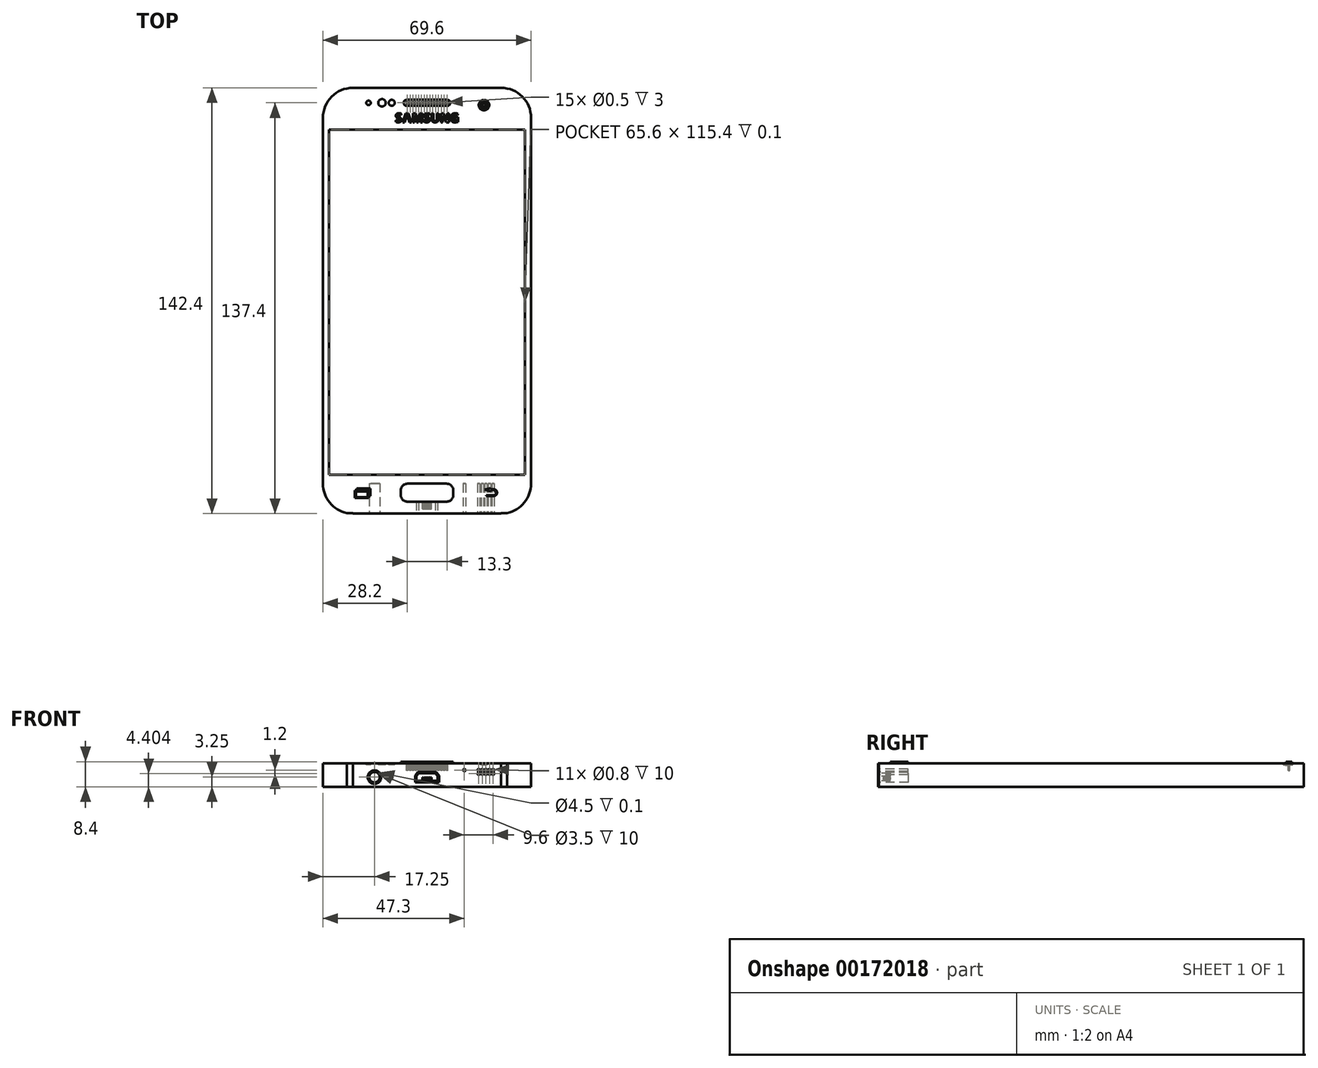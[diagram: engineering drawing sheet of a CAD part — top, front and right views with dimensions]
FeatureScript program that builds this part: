
annotation { "Feature Type Name" : "Feature", "Feature Type Description" : "" }
export const myFeature = defineFeature(function(context is Context, id is Id, definition is map)
    precondition{}
    {
        {
            var Q0;
            Q0=qCreatedBy(makeId("Top.planeOp"),FACE);
            var sketch = newSketch(context, id + "F0", { "sketchPlane" : qUnion([Q0])});
            skLineSegment(sketch, "E0.bottom", {"start": v(0, 0) * mm, "end": v(69.6, 0) * mm});
            skLineSegment(sketch, "E0.top", {"start": v(0, -142.4) * mm, "end": v(69.6, -142.4) * mm});
            skLineSegment(sketch, "E0.left", {"start": v(0, 0) * mm, "end": v(0, -142.4) * mm});
            skLineSegment(sketch, "E0.right", {"start": v(69.6, 0) * mm, "end": v(69.6, -142.4) * mm});
            skSolve(sketch);
        }
        {
            var Q0;
            Q0 = qSketchRegion(id + "F0", true);
            extrude(context, id + "F1", {"entities" : qUnion([Q0]), "depth" : 7.9 * mm});
        }
        {
            var Q0;
            Q0=makeQuery(id+"F1.opExtrude","SWEPT_EDGE",EDGE,{"disambiguationData":[OSD([sQuery(id+"F0.wireOp",EDGE,"E0.top"),sQuery(id+"F0.wireOp",EDGE,"E0.right")])]});
            var Q1;
            Q1=makeQuery(id+"F1.opExtrude","SWEPT_EDGE",EDGE,{"disambiguationData":[OSD([sQuery(id+"F0.wireOp",EDGE,"E0.top"),sQuery(id+"F0.wireOp",EDGE,"E0.left")])]});
            var Q2;
            Q2=makeQuery(id+"F1.opExtrude","SWEPT_EDGE",EDGE,{"disambiguationData":[OSD([sQuery(id+"F0.wireOp",EDGE,"E0.bottom"),sQuery(id+"F0.wireOp",EDGE,"E0.right")])]});
            var Q3;
            Q3=makeQuery(id+"F1.opExtrude","SWEPT_EDGE",EDGE,{"disambiguationData":[OSD([sQuery(id+"F0.wireOp",EDGE,"E0.bottom"),sQuery(id+"F0.wireOp",EDGE,"E0.left")])]});
            fillet(context, id + "F2", {"entities" : qUnion([Q0, Q1, Q2, Q3]), "radius" : 10 * mm, "tangentPropagation" : true, "allowEdgeOverflow" : false});
        }
        {
            var Q0;
            Q0=makeQuery(id+"F1.opExtrude","CAP_FACE",FACE,{"disambiguationData":[OSD([sQuery(id+"F0.wireOp",EDGE,"E0.bottom"),sQuery(id+"F0.wireOp",EDGE,"E0.top"),sQuery(id+"F0.wireOp",EDGE,"E0.left"),sQuery(id+"F0.wireOp",EDGE,"E0.right")])],"isStart":false});
            var sketch = newSketch(context, id + "F3", { "sketchPlane" : qUnion([Q0])});
            skLineSegment(sketch, "E1.bottom", {"start": v(2, -14) * mm, "end": v(67.6, -14) * mm});
            skLineSegment(sketch, "E1.top", {"start": v(2, -129.4) * mm, "end": v(67.6, -129.4) * mm});
            skLineSegment(sketch, "E1.left", {"start": v(2, -14) * mm, "end": v(2, -129.4) * mm});
            skLineSegment(sketch, "E1.right", {"start": v(67.6, -14) * mm, "end": v(67.6, -129.4) * mm});
            skSolve(sketch);
        }
        {
            var Q0;
            Q0=makeQuery(id+"F3.imprint","IMPRINT",FACE,{"disambiguationData":[TD([[makeQuery(id+"F3.imprint","IMPRINT",EDGE,{"derivedFrom":sQuery(id+"F3.wireOp",EDGE,"E1.bottom")}),1.0]])]});
            var sketch = newSketch(context, id + "F4", { "sketchPlane" : qUnion([Q0])});
            skLineSegment(sketch, "E2.bottom", {"start": v(26, -132.4) * mm, "end": v(43.6, -132.4) * mm});
            skLineSegment(sketch, "E2.top", {"start": v(26, -138.4) * mm, "end": v(43.6, -138.4) * mm});
            skLineSegment(sketch, "E2.left", {"start": v(26, -132.4) * mm, "end": v(26, -138.4) * mm});
            skLineSegment(sketch, "E2.right", {"start": v(43.6, -132.4) * mm, "end": v(43.6, -138.4) * mm});
            skSolve(sketch);
        }
        {
            var Q0;
            Q0 = qSketchRegion(id + "F4", true);
            extrude(context, id + "F5", {"entities" : qUnion([Q0]), "operationType" : NewBodyOperationType.ADD, "depth" : 0.5 * mm});
        }
        {
            var Q0;
            Q0=makeQuery(id+"F5.opExtrude","SWEPT_EDGE",EDGE,{"disambiguationData":[OSD([sQuery(id+"F4.wireOp",EDGE,"E2.bottom"),sQuery(id+"F4.wireOp",EDGE,"E2.left")])]});
            var Q1;
            Q1=makeQuery(id+"F5.opExtrude","SWEPT_EDGE",EDGE,{"disambiguationData":[OSD([sQuery(id+"F4.wireOp",EDGE,"E2.bottom"),sQuery(id+"F4.wireOp",EDGE,"E2.right")])]});
            var Q2;
            Q2=makeQuery(id+"F5.opExtrude","SWEPT_EDGE",EDGE,{"disambiguationData":[OSD([sQuery(id+"F4.wireOp",EDGE,"E2.top"),sQuery(id+"F4.wireOp",EDGE,"E2.left")])]});
            var Q3;
            Q3=makeQuery(id+"F5.opExtrude","SWEPT_EDGE",EDGE,{"disambiguationData":[OSD([sQuery(id+"F4.wireOp",EDGE,"E2.top"),sQuery(id+"F4.wireOp",EDGE,"E2.right")])]});
            fillet(context, id + "F6", {"entities" : qUnion([Q0, Q1, Q2, Q3]), "radius" : 2.25 * mm, "tangentPropagation" : true, "allowEdgeOverflow" : false});
        }
        {
            var Q0;
            Q0 = qSketchRegion(id + "F3", true);
            extrude(context, id + "F7", {"entities" : qUnion([Q0]), "operationType" : NewBodyOperationType.REMOVE, "oppositeDirection" : true, "depth" : 0.1 * mm});
        }
        {
            var Q0;
            Q0=makeQuery(id+"F1.opExtrude","CAP_FACE",FACE,{"disambiguationData":[OSD([sQuery(id+"F0.wireOp",EDGE,"E0.bottom"),sQuery(id+"F0.wireOp",EDGE,"E0.top"),sQuery(id+"F0.wireOp",EDGE,"E0.left"),sQuery(id+"F0.wireOp",EDGE,"E0.right")])],"isStart":false});
            var sketch = newSketch(context, id + "F8", { "sketchPlane" : qUnion([Q0])});
            skLineSegment(sketch, "E3.bottom", {"start": v(27, -4) * mm, "end": v(42.6, -4) * mm});
            skLineSegment(sketch, "E3.top", {"start": v(27, -6) * mm, "end": v(42.6, -6) * mm});
            skLineSegment(sketch, "E3.left", {"start": v(27, -4) * mm, "end": v(27, -6) * mm});
            skLineSegment(sketch, "E3.right", {"start": v(42.6, -4) * mm, "end": v(42.6, -6) * mm});
            skSolve(sketch);
        }
        {
            var Q0;
            Q0 = qSketchRegion(id + "F8", true);
            extrude(context, id + "F9", {"entities" : qUnion([Q0]), "operationType" : NewBodyOperationType.ADD, "depth" : 0.5 * mm});
        }
        {
            var Q0;
            Q0=makeQuery(id+"F9.opExtrude","SWEPT_EDGE",EDGE,{"disambiguationData":[OSD([sQuery(id+"F8.wireOp",EDGE,"E3.bottom"),sQuery(id+"F8.wireOp",EDGE,"E3.right")])]});
            var Q1;
            Q1=makeQuery(id+"F9.opExtrude","SWEPT_EDGE",EDGE,{"disambiguationData":[OSD([sQuery(id+"F8.wireOp",EDGE,"E3.bottom"),sQuery(id+"F8.wireOp",EDGE,"E3.left")])]});
            var Q2;
            Q2=makeQuery(id+"F9.opExtrude","SWEPT_EDGE",EDGE,{"disambiguationData":[OSD([sQuery(id+"F8.wireOp",EDGE,"E3.top"),sQuery(id+"F8.wireOp",EDGE,"E3.right")])]});
            var Q3;
            Q3=makeQuery(id+"F9.opExtrude","SWEPT_EDGE",EDGE,{"disambiguationData":[OSD([sQuery(id+"F8.wireOp",EDGE,"E3.top"),sQuery(id+"F8.wireOp",EDGE,"E3.left")])]});
            fillet(context, id + "F10", {"entities" : qUnion([Q0, Q1, Q2, Q3]), "radius" : 1 * mm, "tangentPropagation" : true, "allowEdgeOverflow" : false});
        }
        {
            var Q0;
            Q0=makeQuery(id+"F1.opExtrude","CAP_FACE",FACE,{"disambiguationData":[OSD([sQuery(id+"F0.wireOp",EDGE,"E0.bottom"),sQuery(id+"F0.wireOp",EDGE,"E0.top"),sQuery(id+"F0.wireOp",EDGE,"E0.left"),sQuery(id+"F0.wireOp",EDGE,"E0.right")])],"isStart":false});
            var sketch = newSketch(context, id + "F11", { "sketchPlane" : qUnion([Q0])});
            skCircle(sketch, "E4", {"center": v(23, -5) * mm, "radius": 1 * mm});
            skCircle(sketch, "E5", {"center": v(19.75, -5) * mm, "radius": 1.25 * mm});
            skCircle(sketch, "E6", {"center": v(15.25, -5) * mm, "radius": 0.75 * mm});
            skSolve(sketch);
        }
        {
            var Q0;
            Q0 = qSketchRegion(id + "F11", true);
            extrude(context, id + "F12", {"entities" : qUnion([Q0]), "operationType" : NewBodyOperationType.REMOVE, "oppositeDirection" : true, "depth" : 0.5 * mm});
        }
        {
            var Q0;
            Q0=makeQuery(id+"F9.opExtrude","CAP_FACE",FACE,{"disambiguationData":[OSD([sQuery(id+"F8.wireOp",EDGE,"E3.bottom"),sQuery(id+"F8.wireOp",EDGE,"E3.top"),sQuery(id+"F8.wireOp",EDGE,"E3.left"),sQuery(id+"F8.wireOp",EDGE,"E3.right")])],"isStart":false});
            var sketch = newSketch(context, id + "F13", { "sketchPlane" : qUnion([Q0])});
            skCircle(sketch, "E7", {"center": v(28.2, -5) * mm, "radius": 0.25 * mm});
            skPoint(sketch, "E7.centerSnap0", {"position": v(28.2, -4) * mm});
            skPoint(sketch, "E7.centerSnap1", {"position": v(27, -5) * mm});
            skCircle(sketch, "E8.1.0.0", {"center": v(29.15, -5) * mm, "radius": 0.25 * mm});
            skCircle(sketch, "E8.2.0.0", {"center": v(30.1, -5) * mm, "radius": 0.25 * mm});
            skCircle(sketch, "E8.3.0.0", {"center": v(31.05, -5) * mm, "radius": 0.25 * mm});
            skCircle(sketch, "E8.4.0.0", {"center": v(32, -5) * mm, "radius": 0.25 * mm});
            skCircle(sketch, "E8.5.0.0", {"center": v(32.95, -5) * mm, "radius": 0.25 * mm});
            skCircle(sketch, "E8.6.0.0", {"center": v(33.9, -5) * mm, "radius": 0.25 * mm});
            skCircle(sketch, "E8.7.0.0", {"center": v(34.85, -5) * mm, "radius": 0.25 * mm});
            skCircle(sketch, "E8.8.0.0", {"center": v(35.8, -5) * mm, "radius": 0.25 * mm});
            skCircle(sketch, "E8.9.0.0", {"center": v(36.75, -5) * mm, "radius": 0.25 * mm});
            skCircle(sketch, "E8.10.0.0", {"center": v(37.7, -5) * mm, "radius": 0.25 * mm});
            skCircle(sketch, "E8.11.0.0", {"center": v(38.65, -5) * mm, "radius": 0.25 * mm});
            skCircle(sketch, "E8.12.0.0", {"center": v(39.6, -5) * mm, "radius": 0.25 * mm});
            skCircle(sketch, "E8.13.0.0", {"center": v(40.55, -5) * mm, "radius": 0.25 * mm});
            skCircle(sketch, "E8.14.0.0", {"center": v(41.5, -5) * mm, "radius": 0.25 * mm});
            skLineSegment(sketch, "E8.direction1", {"start": v(28.2, -5) * mm, "end": v(29.15, -5) * mm, "construction": true});
            skSolve(sketch);
        }
        {
            var Q0;
            Q0 = qSketchRegion(id + "F13", true);
            extrude(context, id + "F14", {"entities" : qUnion([Q0]), "operationType" : NewBodyOperationType.REMOVE, "oppositeDirection" : true, "depth" : 3 * mm});
        }
        {
            var Q0;
            Q0=makeQuery(id+"F1.opExtrude","CAP_FACE",FACE,{"disambiguationData":[OSD([sQuery(id+"F0.wireOp",EDGE,"E0.bottom"),sQuery(id+"F0.wireOp",EDGE,"E0.top"),sQuery(id+"F0.wireOp",EDGE,"E0.left"),sQuery(id+"F0.wireOp",EDGE,"E0.right")])],"isStart":false});
            var sketch = newSketch(context, id + "F15", { "sketchPlane" : qUnion([Q0])});
            skCircle(sketch, "E9", {"center": v(53.85, -5.75) * mm, "radius": 1.75 * mm});
            skSolve(sketch);
        }
        {
            var Q0;
            Q0 = qSketchRegion(id + "F15", true);
            extrude(context, id + "F16", {"entities" : qUnion([Q0]), "operationType" : NewBodyOperationType.REMOVE, "oppositeDirection" : true, "depth" : 0.1 * mm});
        }
        {
            var Q0;
            Q0=makeQuery(id+"F16.boolean.opBoolean","COPY",FACE,{"derivedFrom":makeQuery(id+"F16.opExtrude","CAP_FACE",FACE,{"disambiguationData":[OSD([sQuery(id+"F15.wireOp",EDGE,"E9")])],"isStart":false})});
            var sketch = newSketch(context, id + "F17", { "sketchPlane" : qUnion([Q0])});
            skCircle(sketch, "E10", {"center": v(53.85, -5.75) * mm, "radius": 1.13 * mm});
            skSolve(sketch);
        }
        {
            var Q0;
            Q0 = qSketchRegion(id + "F17", true);
            extrude(context, id + "F18", {"entities" : qUnion([Q0]), "operationType" : NewBodyOperationType.REMOVE, "oppositeDirection" : true, "depth" : 0.5 * mm});
        }
        {
            var Q0;
            Q0=makeQuery(id+"F18.boolean.opBoolean","COPY",FACE,{"derivedFrom":makeQuery(id+"F18.opExtrude","CAP_FACE",FACE,{"disambiguationData":[OSD([sQuery(id+"F17.wireOp",EDGE,"E10")])],"isStart":false})});
            var sketch = newSketch(context, id + "F19", { "sketchPlane" : qUnion([Q0])});
            skCircle(sketch, "E11", {"center": v(53.85, -5.75) * mm, "radius": 0.5 * mm});
            skSolve(sketch);
        }
        {
            var Q0;
            Q0 = qSketchRegion(id + "F19", true);
            extrude(context, id + "F20", {"entities" : qUnion([Q0]), "operationType" : NewBodyOperationType.REMOVE, "oppositeDirection" : true, "depth" : 0.1 * mm});
        }
        {
            var Q0;
            Q0=makeQuery(id+"F1.opExtrude","CAP_FACE",FACE,{"disambiguationData":[OSD([sQuery(id+"F0.wireOp",EDGE,"E0.bottom"),sQuery(id+"F0.wireOp",EDGE,"E0.top"),sQuery(id+"F0.wireOp",EDGE,"E0.left"),sQuery(id+"F0.wireOp",EDGE,"E0.right")])],"isStart":false});
            var sketch = newSketch(context, id + "F21", { "sketchPlane" : qUnion([Q0])});
            skText(sketch, "E12", { "text": "S   MSUNG", "fontName": "OpenSans-Bold.ttf"});
            const initialGuessF21  = {"E12": [0.02417, -0.0115, 1, 0, 0.003]};
            skSetInitialGuess(sketch, initialGuessF21);
            skSolve(sketch);
        }
        {
            var Q0;
            Q0 = qSketchRegion(id + "F21", true);
            extrude(context, id + "F22", {"entities" : qUnion([Q0]), "operationType" : NewBodyOperationType.REMOVE, "oppositeDirection" : true, "depth" : 0.1 * mm});
        }
        {
            var Q0;
            Q0=makeQuery(id+"F1.opExtrude","CAP_FACE",FACE,{"disambiguationData":[OSD([sQuery(id+"F0.wireOp",EDGE,"E0.bottom"),sQuery(id+"F0.wireOp",EDGE,"E0.top"),sQuery(id+"F0.wireOp",EDGE,"E0.left"),sQuery(id+"F0.wireOp",EDGE,"E0.right")])],"isStart":false});
            var sketch = newSketch(context, id + "F23", { "sketchPlane" : qUnion([Q0])});
            skLineSegment(sketch, "E13", {"start": v(27.67, -8.53) * mm, "end": v(28.62, -8.53) * mm});
            skLineSegment(sketch, "E14", {"start": v(28.62, -8.53) * mm, "end": v(29.59, -11.5) * mm});
            skLineSegment(sketch, "E15", {"start": v(29.59, -11.5) * mm, "end": v(29.01, -11.5) * mm});
            skLineSegment(sketch, "E16", {"start": v(29.01, -11.5) * mm, "end": v(28.15, -8.84) * mm});
            skLineSegment(sketch, "E17", {"start": v(28.15, -8.84) * mm, "end": v(27.28, -11.5) * mm});
            skLineSegment(sketch, "E18", {"start": v(27.28, -11.5) * mm, "end": v(26.7, -11.5) * mm});
            skLineSegment(sketch, "E19", {"start": v(26.7, -11.5) * mm, "end": v(27.67, -8.53) * mm});
            skSolve(sketch);
        }
        {
            var Q0;
            Q0 = qSketchRegion(id + "F23", true);
            extrude(context, id + "F24", {"entities" : qUnion([Q0]), "operationType" : NewBodyOperationType.REMOVE, "oppositeDirection" : true, "depth" : 0.1 * mm});
        }
        {
            var Q0;
            Q0=makeQuery(id+"F1.opExtrude","CAP_FACE",FACE,{"disambiguationData":[OSD([sQuery(id+"F0.wireOp",EDGE,"E0.bottom"),sQuery(id+"F0.wireOp",EDGE,"E0.top"),sQuery(id+"F0.wireOp",EDGE,"E0.left"),sQuery(id+"F0.wireOp",EDGE,"E0.right")])],"isStart":false});
            var sketch = newSketch(context, id + "F25", { "sketchPlane" : qUnion([Q0])});
            skLineSegment(sketch, "E20.bottom", {"start": v(10.7, -134.65) * mm, "end": v(15.3, -134.65) * mm});
            skLineSegment(sketch, "E20.top", {"start": v(10.7, -137.17) * mm, "end": v(15.3, -137.17) * mm});
            skLineSegment(sketch, "E20.left", {"start": v(10.7, -134.65) * mm, "end": v(10.7, -137.17) * mm});
            skLineSegment(sketch, "E20.right", {"start": v(15.3, -134.65) * mm, "end": v(15.3, -137.17) * mm});
            skLineSegment(sketch, "E21.bottom", {"start": v(11, -134.95) * mm, "end": v(15, -134.95) * mm});
            skLineSegment(sketch, "E21.top", {"start": v(11, -136.88) * mm, "end": v(15, -136.88) * mm});
            skLineSegment(sketch, "E21.left", {"start": v(11, -134.95) * mm, "end": v(11, -136.88) * mm});
            skLineSegment(sketch, "E21.right", {"start": v(15, -134.95) * mm, "end": v(15, -136.88) * mm});
            skLineSegment(sketch, "E22.bottom", {"start": v(11.3, -134.05) * mm, "end": v(15.9, -134.05) * mm});
            skLineSegment(sketch, "E22.top", {"start": v(11.3, -134.35) * mm, "end": v(15.6, -134.35) * mm});
            skLineSegment(sketch, "E22.left", {"start": v(11.3, -134.05) * mm, "end": v(11.3, -134.35) * mm});
            skLineSegment(sketch, "E23.top", {"start": v(15.9, -136.57) * mm, "end": v(15.6, -136.57) * mm});
            skLineSegment(sketch, "E23.right", {"start": v(15.6, -134.35) * mm, "end": v(15.6, -136.57) * mm});
            skLineSegment(sketch, "E24", {"start": v(15.9, -134.05) * mm, "end": v(15.9, -136.57) * mm});
            skSolve(sketch);
        }
        {
            var Q0;
            Q0 = qSketchRegion(id + "F25", true);
            extrude(context, id + "F26", {"entities" : qUnion([Q0]), "operationType" : NewBodyOperationType.REMOVE, "oppositeDirection" : true, "depth" : 0.1 * mm});
        }
        {
            var Q0;
            {var subQ1=sQuery(id+"F0.wireOp",EDGE,"E0.left");var subQ2=sQuery(id+"F0.wireOp",EDGE,"E0.bottom");var subQ5=sQuery(id+"F0.wireOp",EDGE,"E0.right");var subQ9=sQuery(id+"F0.wireOp",EDGE,"E0.top");Q0=makeQuery(id+"F26.boolean.opBoolean","SPLIT",FACE,{"disambiguationData":[TD([makeQuery(id+"F1.opExtrude","SWEPT_FACE",FACE,{"disambiguationData":[OSD([subQ2])]})])],"derivedFrom":makeQuery(id+"F1.opExtrude","CAP_FACE",FACE,{"disambiguationData":[OSD([subQ2,subQ9,subQ1,subQ5])],"isStart":false})});}
            var sketch = newSketch(context, id + "F27", { "sketchPlane" : qUnion([Q0])});
            skLineSegment(sketch, "E25", {"start": v(54.6, -136.25) * mm, "end": v(57.1, -136.25) * mm});
            skArc(sketch, "E26", {"start": v(57.1, -136.25) * mm, "mid": v(57.95, -135.4) * mm, "end": v(57.1, -134.55) * mm});
            skPoint(sketch, "E26.endSnap0", {"position": v(42.94, -133.06) * mm});
            skLineSegment(sketch, "E27", {"start": v(57.1, -134.55) * mm, "end": v(56.1, -134.55) * mm});
            skLineSegment(sketch, "E28", {"start": v(56.1, -134.25) * mm, "end": v(57.1, -134.25) * mm});
            skLineSegment(sketch, "E29", {"start": v(54.6, -136.55) * mm, "end": v(57.1, -136.55) * mm});
            skArc(sketch, "E30", {"start": v(57.1, -136.55) * mm, "mid": v(58.25, -135.4) * mm, "end": v(57.1, -134.25) * mm});
            skLineSegment(sketch, "E31", {"start": v(54.6, -136.55) * mm, "end": v(54.6, -136.25) * mm});
            skLineSegment(sketch, "E32", {"start": v(56.1, -134.25) * mm, "end": v(56.1, -133.85) * mm});
            skLineSegment(sketch, "E33", {"start": v(56.1, -133.85) * mm, "end": v(54.1, -134.4) * mm});
            skLineSegment(sketch, "E34", {"start": v(54.1, -134.4) * mm, "end": v(56.1, -134.95) * mm});
            skLineSegment(sketch, "E35", {"start": v(56.1, -134.95) * mm, "end": v(56.1, -134.55) * mm});
            skSolve(sketch);
        }
        {
            var Q0;
            Q0 = qSketchRegion(id + "F27", true);
            extrude(context, id + "F28", {"entities" : qUnion([Q0]), "operationType" : NewBodyOperationType.REMOVE, "oppositeDirection" : true, "depth" : 0.1 * mm});
        }
        {
            var Q0;
            Q0=makeQuery(id+"F1.opExtrude","SWEPT_FACE",FACE,{"disambiguationData":[OSD([sQuery(id+"F0.wireOp",EDGE,"E0.top")])]});
            var sketch = newSketch(context, id + "F29", { "sketchPlane" : qUnion([Q0])});
            skCircle(sketch, "E36", {"center": v(17.25, 3.25) * mm, "radius": 2.25 * mm});
            skSolve(sketch);
        }
        {
            var Q0;
            Q0 = qSketchRegion(id + "F29", true);
            extrude(context, id + "F30", {"entities" : qUnion([Q0]), "operationType" : NewBodyOperationType.REMOVE, "oppositeDirection" : true, "depth" : 0.1 * mm});
        }
        {
            var Q0;
            Q0=makeQuery(id+"F30.boolean.opBoolean","COPY",FACE,{"derivedFrom":makeQuery(id+"F30.opExtrude","CAP_FACE",FACE,{"disambiguationData":[OSD([sQuery(id+"F29.wireOp",EDGE,"E36")])],"isStart":false})});
            var sketch = newSketch(context, id + "F31", { "sketchPlane" : qUnion([Q0])});
            skCircle(sketch, "E37", {"center": v(17.25, 3.25) * mm, "radius": 1.75 * mm});
            skSolve(sketch);
        }
        {
            var Q0;
            Q0 = qSketchRegion(id + "F31", true);
            extrude(context, id + "F32", {"entities" : qUnion([Q0]), "operationType" : NewBodyOperationType.REMOVE, "oppositeDirection" : true, "depth" : 10 * mm});
        }
        {
            var Q0;
            Q0=makeQuery(id+"F1.opExtrude","SWEPT_FACE",FACE,{"disambiguationData":[OSD([sQuery(id+"F0.wireOp",EDGE,"E0.top")])]});
            var sketch = newSketch(context, id + "F33", { "sketchPlane" : qUnion([Q0])});
            skLineSegment(sketch, "E38.bottom", {"start": v(10, 7.9) * mm, "end": v(8, 7.9) * mm});
            skLineSegment(sketch, "E38.top", {"start": v(10, 0) * mm, "end": v(8, 0) * mm});
            skLineSegment(sketch, "E38.left", {"start": v(10, 7.9) * mm, "end": v(10, 0) * mm});
            skLineSegment(sketch, "E38.right", {"start": v(8, 7.9) * mm, "end": v(8, 0) * mm});
            skLineSegment(sketch, "E39.bottom", {"start": v(59.6, 7.9) * mm, "end": v(61.6, 7.9) * mm});
            skLineSegment(sketch, "E39.top", {"start": v(59.6, 0) * mm, "end": v(61.6, 0) * mm});
            skLineSegment(sketch, "E39.left", {"start": v(59.6, 7.9) * mm, "end": v(59.6, 0) * mm});
            skLineSegment(sketch, "E39.right", {"start": v(61.6, 7.9) * mm, "end": v(61.6, 0) * mm});
            skSolve(sketch);
        }
        {
            var Q0;
            Q0 = qSketchRegion(id + "F33", true);
            extrude(context, id + "F34", {"entities" : qUnion([Q0]), "operationType" : NewBodyOperationType.REMOVE, "oppositeDirection" : true, "depth" : 0.2 * mm});
        }
        {
            var Q0;
            Q0=makeQuery(id+"F1.opExtrude","SWEPT_FACE",FACE,{"disambiguationData":[OSD([sQuery(id+"F0.wireOp",EDGE,"E0.top")])]});
            var sketch = newSketch(context, id + "F35", { "sketchPlane" : qUnion([Q0])});
            skLineSegment(sketch, "E40", {"start": v(30.8, 1.5) * mm, "end": v(38.8, 1.5) * mm});
            skLineSegment(sketch, "E41", {"start": v(38.8, 1.5) * mm, "end": v(38.8, 3.75) * mm});
            skLineSegment(sketch, "E42", {"start": v(38.8, 3.75) * mm, "end": v(37.8, 5) * mm});
            skLineSegment(sketch, "E43", {"start": v(37.8, 5) * mm, "end": v(31.8, 5) * mm});
            skLineSegment(sketch, "E44", {"start": v(31.8, 5) * mm, "end": v(30.8, 3.75) * mm});
            skLineSegment(sketch, "E45", {"start": v(30.8, 3.75) * mm, "end": v(30.8, 1.5) * mm});
            skPoint(sketch, "E46", {"position": v(34.8, 5) * mm});
            skPoint(sketch, "E47", {"position": v(34.8, 1.5) * mm});
            skSolve(sketch);
        }
        {
            var Q0;
            Q0 = qSketchRegion(id + "F35", true);
            extrude(context, id + "F36", {"entities" : qUnion([Q0]), "operationType" : NewBodyOperationType.REMOVE, "oppositeDirection" : true, "depth" : 0.1 * mm});
        }
        {
            var Q0;
            Q0=makeQuery(id+"F36.boolean.opBoolean","COPY",FACE,{"derivedFrom":makeQuery(id+"F36.opExtrude","CAP_FACE",FACE,{"disambiguationData":[OSD([sQuery(id+"F35.wireOp",EDGE,"E40"),sQuery(id+"F35.wireOp",EDGE,"E41"),sQuery(id+"F35.wireOp",EDGE,"E42"),sQuery(id+"F35.wireOp",EDGE,"E43"),sQuery(id+"F35.wireOp",EDGE,"E44"),sQuery(id+"F35.wireOp",EDGE,"E45")])],"isStart":false})});
            var sketch = newSketch(context, id + "F37", { "sketchPlane" : qUnion([Q0])});
            skLineSegment(sketch, "E48", {"start": v(31.3, 2) * mm, "end": v(31.3, 3.57) * mm});
            skLineSegment(sketch, "E49", {"start": v(31.3, 3.57) * mm, "end": v(32.04, 4.5) * mm});
            skLineSegment(sketch, "E50", {"start": v(32.04, 4.5) * mm, "end": v(37.56, 4.5) * mm});
            skLineSegment(sketch, "E51", {"start": v(37.56, 4.5) * mm, "end": v(38.3, 3.57) * mm});
            skLineSegment(sketch, "E52", {"start": v(38.3, 3.57) * mm, "end": v(38.3, 2) * mm});
            skLineSegment(sketch, "E53", {"start": v(38.3, 2) * mm, "end": v(31.3, 2) * mm});
            skSolve(sketch);
        }
        {
            var Q0;
            Q0 = qSketchRegion(id + "F37", true);
            extrude(context, id + "F38", {"entities" : qUnion([Q0]), "operationType" : NewBodyOperationType.REMOVE, "oppositeDirection" : true, "depth" : 4 * mm});
        }
        {
            var Q0;
            Q0=makeQuery(id+"F38.boolean.opBoolean","COPY",FACE,{"derivedFrom":makeQuery(id+"F38.opExtrude","CAP_FACE",FACE,{"disambiguationData":[OSD([sQuery(id+"F37.wireOp",EDGE,"E48"),sQuery(id+"F37.wireOp",EDGE,"E49"),sQuery(id+"F37.wireOp",EDGE,"E50"),sQuery(id+"F37.wireOp",EDGE,"E51"),sQuery(id+"F37.wireOp",EDGE,"E52"),sQuery(id+"F37.wireOp",EDGE,"E53")])],"isStart":false})});
            var sketch = newSketch(context, id + "F39", { "sketchPlane" : qUnion([Q0])});
            skLineSegment(sketch, "E54", {"start": v(33.3, 2.5) * mm, "end": v(36.3, 2.5) * mm});
            skLineSegment(sketch, "E55", {"start": v(36.3, 2.5) * mm, "end": v(36.3, 3.2) * mm});
            skLineSegment(sketch, "E56", {"start": v(36.3, 3.2) * mm, "end": v(36.02, 3.2) * mm});
            skLineSegment(sketch, "E57", {"start": v(36.02, 3.2) * mm, "end": v(36.02, 2.95) * mm});
            skLineSegment(sketch, "E58", {"start": v(36.02, 2.95) * mm, "end": v(35.76, 2.95) * mm});
            skLineSegment(sketch, "E59", {"start": v(35.76, 2.95) * mm, "end": v(35.76, 3.2) * mm});
            skLineSegment(sketch, "E60", {"start": v(35.76, 3.2) * mm, "end": v(35.48, 3.2) * mm});
            skLineSegment(sketch, "E61", {"start": v(35.48, 3.2) * mm, "end": v(35.48, 2.95) * mm});
            skLineSegment(sketch, "E62", {"start": v(35.48, 2.95) * mm, "end": v(35.21, 2.95) * mm});
            skLineSegment(sketch, "E63", {"start": v(35.21, 2.95) * mm, "end": v(35.21, 3.2) * mm});
            skLineSegment(sketch, "E64", {"start": v(35.21, 3.2) * mm, "end": v(34.93, 3.2) * mm});
            skLineSegment(sketch, "E65", {"start": v(34.93, 3.2) * mm, "end": v(34.93, 2.95) * mm});
            skLineSegment(sketch, "E66", {"start": v(34.93, 2.95) * mm, "end": v(34.67, 2.95) * mm});
            skLineSegment(sketch, "E67", {"start": v(34.67, 2.95) * mm, "end": v(34.67, 3.2) * mm});
            skLineSegment(sketch, "E68", {"start": v(34.67, 3.2) * mm, "end": v(34.39, 3.2) * mm});
            skLineSegment(sketch, "E69", {"start": v(34.39, 3.2) * mm, "end": v(34.39, 2.95) * mm});
            skLineSegment(sketch, "E70", {"start": v(34.39, 2.95) * mm, "end": v(34.12, 2.95) * mm});
            skLineSegment(sketch, "E71", {"start": v(34.12, 2.95) * mm, "end": v(34.12, 3.2) * mm});
            skLineSegment(sketch, "E72", {"start": v(34.12, 3.2) * mm, "end": v(33.84, 3.2) * mm});
            skLineSegment(sketch, "E73", {"start": v(33.84, 3.2) * mm, "end": v(33.84, 2.95) * mm});
            skLineSegment(sketch, "E74", {"start": v(33.84, 2.95) * mm, "end": v(33.58, 2.95) * mm});
            skLineSegment(sketch, "E75", {"start": v(33.58, 2.95) * mm, "end": v(33.58, 3.2) * mm});
            skLineSegment(sketch, "E76", {"start": v(33.58, 3.2) * mm, "end": v(33.3, 3.2) * mm});
            skLineSegment(sketch, "E77", {"start": v(33.3, 3.2) * mm, "end": v(33.3, 2.5) * mm});
            skPoint(sketch, "E78", {"position": v(34.8, 2) * mm});
            skPoint(sketch, "E79", {"position": v(34.8, 2.5) * mm});
            skSolve(sketch);
        }
        {
            var Q0;
            Q0 = qSketchRegion(id + "F39", true);
            extrude(context, id + "F40", {"entities" : qUnion([Q0]), "operationType" : NewBodyOperationType.ADD, "depth" : 2.5 * mm});
        }
        {
            var Q0;
            Q0=makeQuery(id+"F1.opExtrude","SWEPT_FACE",FACE,{"disambiguationData":[OSD([sQuery(id+"F0.wireOp",EDGE,"E0.top")])]});
            var sketch = newSketch(context, id + "F41", { "sketchPlane" : qUnion([Q0])});
            skCircle(sketch, "E80", {"center": v(56.9, 5.6) * mm, "radius": 0.4 * mm});
            skCircle(sketch, "E81", {"center": v(56.9, 4.4) * mm, "radius": 0.4 * mm});
            skCircle(sketch, "E82.1.0.0", {"center": v(55.7, 5.6) * mm, "radius": 0.4 * mm});
            skCircle(sketch, "E82.1.0.1", {"center": v(55.7, 4.4) * mm, "radius": 0.4 * mm});
            skLineSegment(sketch, "E82.direction1", {"start": v(55.7, 4.4) * mm, "end": v(56.9, 4.4) * mm, "construction": true});
            skCircle(sketch, "E83.0.2.0", {"center": v(54.5, 5.6) * mm, "radius": 0.4 * mm});
            skCircle(sketch, "E83.2.2.0", {"center": v(54.5, 4.4) * mm, "radius": 0.4 * mm});
            skCircle(sketch, "E83.0.3.0", {"center": v(53.3, 5.6) * mm, "radius": 0.4 * mm});
            skCircle(sketch, "E83.2.3.0", {"center": v(53.3, 4.4) * mm, "radius": 0.4 * mm});
            skCircle(sketch, "E83.0.4.0", {"center": v(52.1, 5.6) * mm, "radius": 0.4 * mm});
            skCircle(sketch, "E83.2.4.0", {"center": v(52.1, 4.4) * mm, "radius": 0.4 * mm});
            skCircle(sketch, "E84", {"center": v(47.3, 5.6) * mm, "radius": 0.4 * mm});
            skSolve(sketch);
        }
        {
            var Q0;
            Q0 = qSketchRegion(id + "F41", true);
            extrude(context, id + "F42", {"entities" : qUnion([Q0]), "operationType" : NewBodyOperationType.REMOVE, "oppositeDirection" : true, "depth" : 10 * mm});
        }
    });
